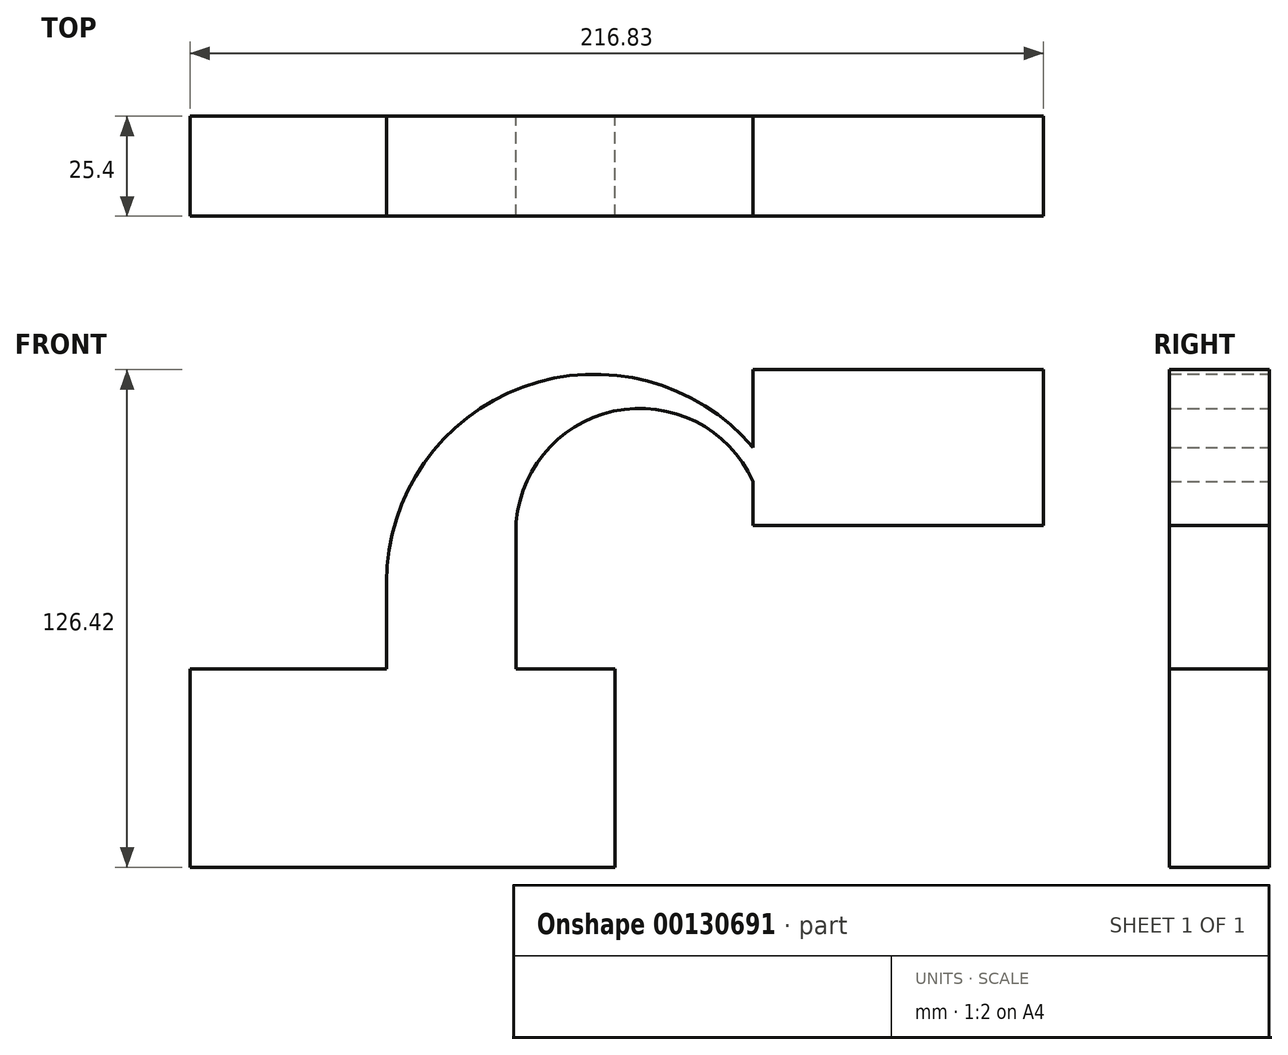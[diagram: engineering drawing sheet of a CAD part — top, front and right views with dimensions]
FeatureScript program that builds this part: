
annotation { "Feature Type Name" : "Feature", "Feature Type Description" : "" }
export const myFeature = defineFeature(function(context is Context, id is Id, definition is map)
    precondition{}
    {
        {
            var Q0;
            Q0=qCreatedBy(makeId("Front.planeOp"),FACE);
            var sketch = newSketch(context, id + "F0", { "sketchPlane" : qUnion([Q0])});
            skLineSegment(sketch, "E0.bottom", {"start": v(-53.98, 20.92) * mm, "end": v(53.98, 20.92) * mm});
            skLineSegment(sketch, "E0.top", {"start": v(-53.98, -29.47) * mm, "end": v(53.98, -29.47) * mm});
            skLineSegment(sketch, "E0.left", {"start": v(-53.98, 20.92) * mm, "end": v(-53.98, -29.47) * mm});
            skLineSegment(sketch, "E0.right", {"start": v(53.98, 20.92) * mm, "end": v(53.98, -29.47) * mm});
            skPoint(sketch, "E0.middle", {"position": v(0, -4.27) * mm});
            skLineSegment(sketch, "E1.bottom", {"start": v(89.07, 57.36) * mm, "end": v(162.85, 57.36) * mm});
            skLineSegment(sketch, "E1.top", {"start": v(89.07, 96.95) * mm, "end": v(162.85, 96.95) * mm});
            skLineSegment(sketch, "E1.left", {"start": v(89.07, 57.36) * mm, "end": v(89.07, 96.95) * mm});
            skLineSegment(sketch, "E1.right", {"start": v(162.85, 57.36) * mm, "end": v(162.85, 96.95) * mm});
            skPoint(sketch, "E1.middle", {"position": v(125.96, 77.15) * mm});
            skLineSegment(sketch, "E2", {"start": v(28.8, 11.47) * mm, "end": v(28.8, 55.56) * mm});
            skLineSegment(sketch, "E3", {"start": v(-4.05, 14.17) * mm, "end": v(-4.05, 42.96) * mm});
            skArc(sketch, "E4", {"start": v(28.8, 55.56) * mm, "mid": v(53.67, 86.4) * mm, "end": v(89.07, 68.6) * mm});
            skArc(sketch, "E5", {"start": v(-4.05, 42.96) * mm, "mid": v(30.58, 92.56) * mm, "end": v(89.07, 77.15) * mm});
            skSolve(sketch);
        }
        {
            var Q0;
            Q0 = qSketchRegion(id + "F0", true);
            extrude(context, id + "F1", {"entities" : qUnion([Q0]), "depth" : 25.4 * mm});
        }
    });
